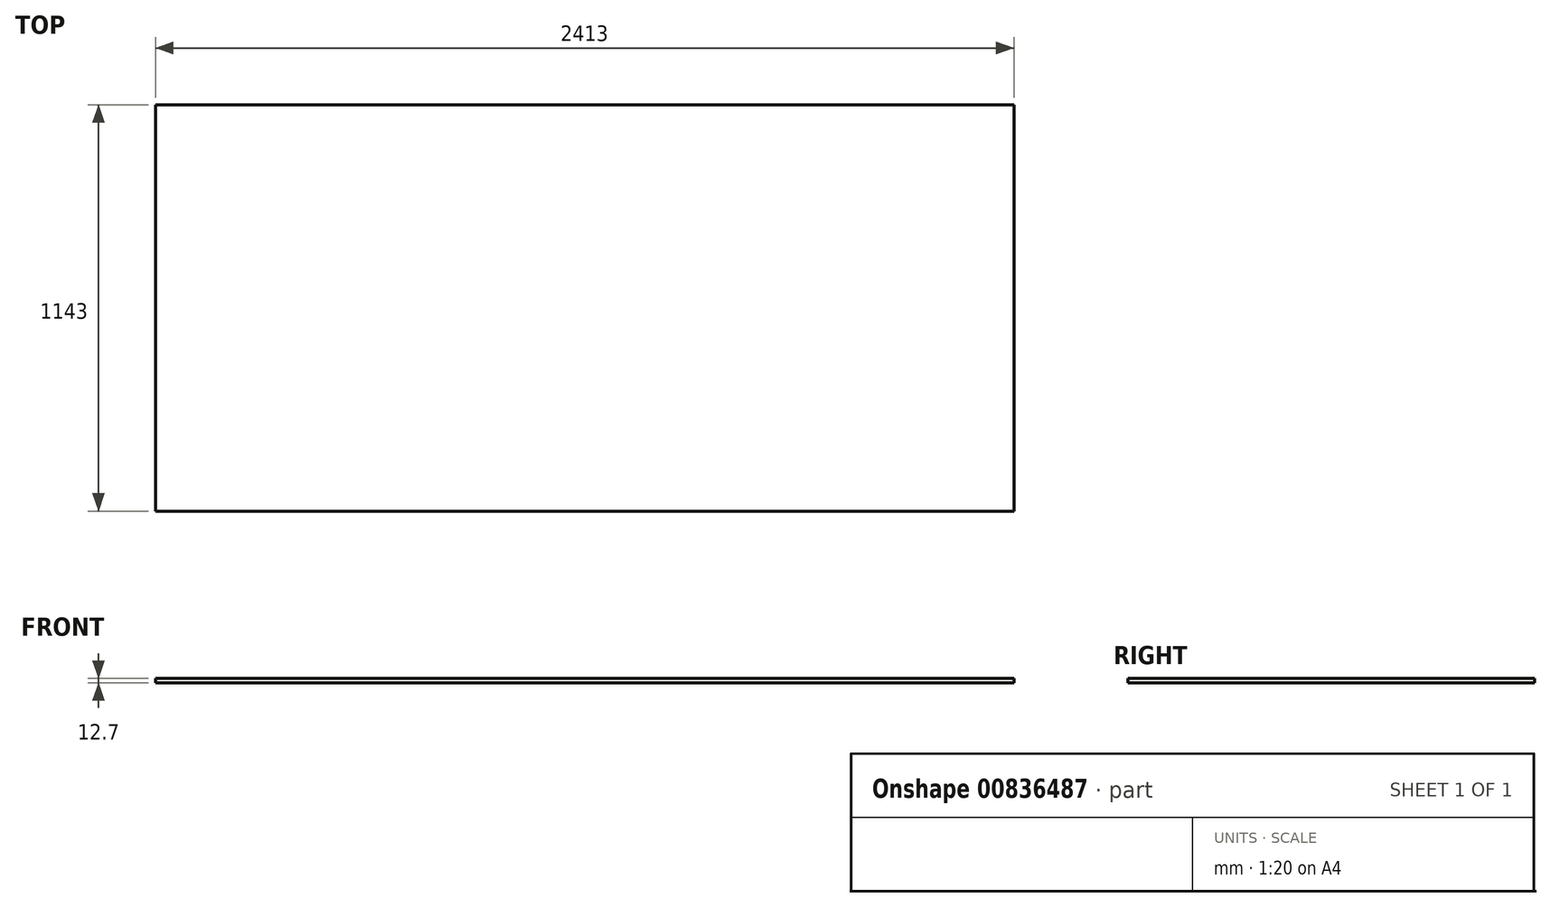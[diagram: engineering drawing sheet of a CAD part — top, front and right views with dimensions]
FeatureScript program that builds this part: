
annotation { "Feature Type Name" : "Feature", "Feature Type Description" : "" }
export const myFeature = defineFeature(function(context is Context, id is Id, definition is map)
    precondition{}
    {
        {
            var Q0;
            Q0=qCreatedBy(makeId("Top.planeOp"),FACE);
            var sketch = newSketch(context, id + "F0", { "sketchPlane" : qUnion([Q0])});
            skLineSegment(sketch, "E0.bottom", {"start": v(0, 0) * mm, "end": v(2413, 0) * mm});
            skLineSegment(sketch, "E0.top", {"start": v(0, 1143) * mm, "end": v(2413, 1143) * mm});
            skLineSegment(sketch, "E0.left", {"start": v(0, 0) * mm, "end": v(0, 1143) * mm});
            skLineSegment(sketch, "E0.right", {"start": v(2413, 0) * mm, "end": v(2413, 1143) * mm});
            skSolve(sketch);
        }
        {
            var Q0;
            Q0=makeQuery(id+"F0.imprint","IMPRINT",FACE,{"disambiguationData":[TD([[makeQuery(id+"F0.imprint","IMPRINT",EDGE,{"derivedFrom":sQuery(id+"F0.wireOp",EDGE,"E0.bottom")}),1.0]])]});
            extrude(context, id + "F1", {"entities" : qUnion([Q0]), "depth" : 12.7 * mm, "offsetDistance" : 25.4 * mm});
        }
    });
